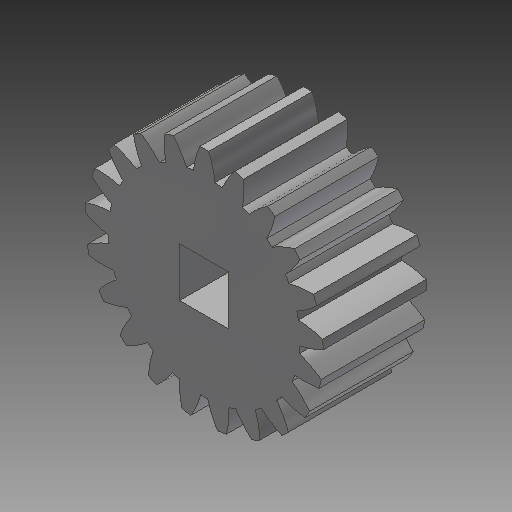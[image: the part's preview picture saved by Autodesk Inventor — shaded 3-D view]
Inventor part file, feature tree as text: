
AUTODESK INVENTOR PART (.ipt)
format: ipt  version: 2017 (Build 210142000, 142)  size: 241,152 bytes
history: native  units: mm (DEFAULTED — no unit token found)
features: plane x3, other x3, sketch x3, extrude x2
ambient origin geometry x8: Origin, YZ Plane, XZ Plane, XY Plane, X Axis, Y Axis, Z Axis, Center Point
bodies: Solid1 (feature_tree)
feature tree (11):
  extrude  "Extrusion1"  Depth=20.0mm TaperAngle=0.0deg
  plane  "Work Plane2"
  plane  "Work Plane8"
  plane  "Work Plane9"
  other  "Spur Gear"
  extrude  "Extrusion2"  Depth=10.0mm TaperAngle=0.0deg
  sketch  "Sketch1"  dims[d0=46.0mm d1=20.0mm d2=0.0mm]
  sketch  "Sketch2"  dims[d3=42.0mm d4=10.0mm d5=0.0mm]
  other  "Srf1"
  sketch  "Sketch3"  dims[d16=80.0mm d17=0.0mm d34=1.495997mm d39=0.0mm d41=0.0mm d43=80.0mm d46=80.0mm d47=0.0mm d48=0.0mm d49=9.525mm d50=10.0mm d51=0.0mm]
  other  "Pitch Diameter"
